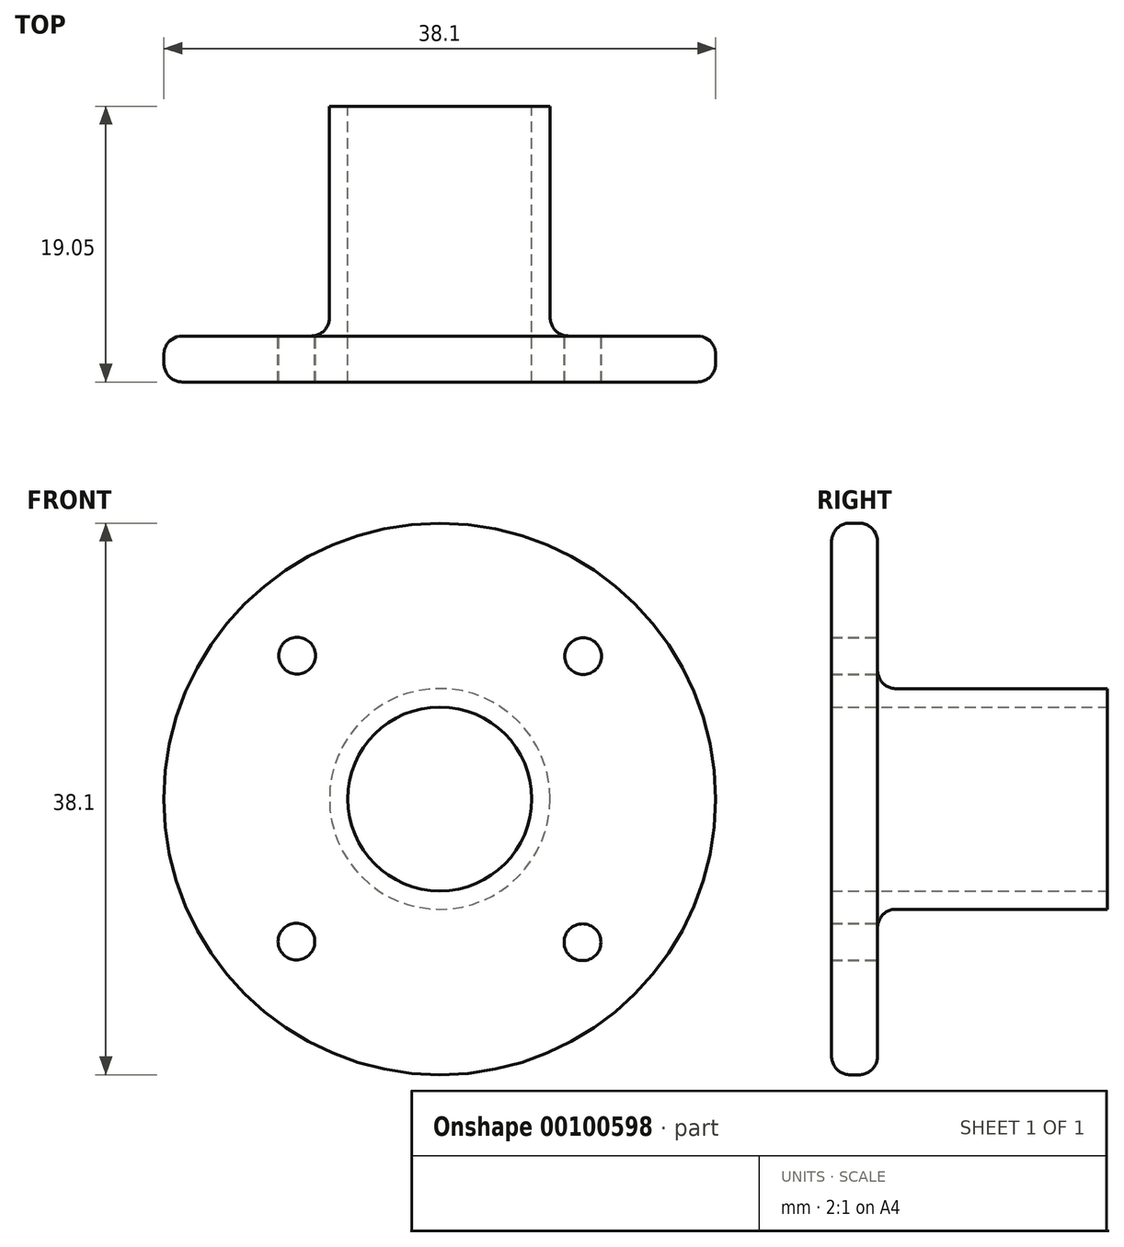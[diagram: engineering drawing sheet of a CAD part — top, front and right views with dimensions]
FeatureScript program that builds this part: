
annotation { "Feature Type Name" : "Feature", "Feature Type Description" : "" }
export const myFeature = defineFeature(function(context is Context, id is Id, definition is map)
    precondition{}
    {
        {
            var Q0;
            Q0=qCreatedBy(makeId("Front.planeOp"),FACE);
            var sketch = newSketch(context, id + "F0", { "sketchPlane" : qUnion([Q0])});
            skCircle(sketch, "E0", {"center": v(0, 0) * mm, "radius": 7.62 * mm});
            skSolve(sketch);
        }
        {
            var Q0;
            Q0=makeQuery(id+"F0.imprint","IMPRINT",FACE,{"disambiguationData":[TD([[makeQuery(id+"F0.imprint","IMPRINT",EDGE,{"derivedFrom":sQuery(id+"F0.wireOp",EDGE,"E0")}),1.0]])]});
            extrude(context, id + "F1", {"entities" : qUnion([Q0]), "depth" : 19.05 * mm});
        }
        {
            var Q0;
            Q0=makeQuery(id+"F1.opExtrude","CAP_FACE",FACE,{"disambiguationData":[OSD([sQuery(id+"F0.wireOp",EDGE,"E0")])],"isStart":false});
            var sketch = newSketch(context, id + "F2", { "sketchPlane" : qUnion([Q0])});
            skCircle(sketch, "E1", {"center": v(0, 0) * mm, "radius": 19.05 * mm});
            skSolve(sketch);
        }
        {
            var Q0;
            Q0=makeQuery(id+"F2.imprint","IMPRINT",FACE,{"disambiguationData":[TD([[makeQuery(id+"F2.imprint","IMPRINT",EDGE,{"derivedFrom":sQuery(id+"F2.wireOp",EDGE,"E1")}),1.0]])]});
            var Q1;
            Q1=makeQuery(id+"F2.imprint","IMPRINT",FACE,{"disambiguationData":[TD([[makeQuery(id+"F2.imprint","IMPRINT",EDGE,{"derivedFrom":makeQuery(id+"F1.opExtrude","CAP_EDGE",EDGE,{"disambiguationData":[OSD([sQuery(id+"F0.wireOp",EDGE,"E0")])],"isStart":false})}),1.0]])]});
            extrude(context, id + "F3", {"entities" : qUnion([Q0, Q1]), "operationType" : NewBodyOperationType.ADD, "oppositeDirection" : true, "depth" : 3.17 * mm});
        }
        {
            var Q0;
            Q0=sQuery(id+"F0.wireOp",VERTEX,"E0.center");
            var Q1;
            Q1=makeQuery(id+"F1.opExtrude","SWEPT_BODY",BODY,{"disambiguationData":[OSD([sQuery(id+"F0.wireOp",EDGE,"E0")])]});
            hole(context, id + "F4", {"style" : HoleStyle.SIMPLE, "endStyle" : HoleEndStyle.THROUGH, "oppositeDirection" : true, "holeDiameter" : 12.7 * mm, "locations" : qUnion([Q0]), "scope" : qUnion([Q1]), "isTappedThrough" : true});
        }
        {
            var Q0;
            Q0=makeQuery(id+"F3.opExtrude","CAP_EDGE",EDGE,{"disambiguationData":[OSD([sQuery(id+"F2.wireOp",EDGE,"E1")])],"isStart":false});
            var Q1;
            Q1=makeQuery(id+"F3.boolean.opBoolean","INTERSECT",EDGE,{"derivedFrom":[makeQuery(id+"F1.opExtrude","SWEPT_FACE",FACE,{"disambiguationData":[OSD([sQuery(id+"F0.wireOp",EDGE,"E0")])]}),makeQuery(id+"F3.opExtrude","CAP_FACE",FACE,{"disambiguationData":[OSD([sQuery(id+"F2.wireOp",EDGE,"E1")])],"isStart":false})]});
            var Q2;
            Q2=makeQuery(id+"F3.opExtrude","CAP_EDGE",EDGE,{"disambiguationData":[OSD([sQuery(id+"F2.wireOp",EDGE,"E1")])],"isStart":true});
            fillet(context, id + "F5", {"entities" : qUnion([Q0, Q1, Q2]), "radius" : 1.27 * mm, "tangentPropagation" : true, "allowEdgeOverflow" : false});
        }
        {
            var Q0;
            Q0=makeQuery(id+"F3.opExtrude","CAP_FACE",FACE,{"disambiguationData":[OSD([sQuery(id+"F2.wireOp",EDGE,"E1")])],"isStart":false});
            var sketch = newSketch(context, id + "F6", { "sketchPlane" : qUnion([Q0])});
            skPoint(sketch, "E2", {"position": v(-9.9, 9.86) * mm});
            skPoint(sketch, "E3.1.0", {"position": v(9.86, 9.9) * mm});
            skPoint(sketch, "E3.2.0", {"position": v(9.9, -9.86) * mm});
            skPoint(sketch, "E3.3.0", {"position": v(-9.86, -9.9) * mm});
            skPoint(sketch, "E3.center", {"position": v(0, 0) * mm});
            skLineSegment(sketch, "E3.anchor1", {"start": v(0, 0) * mm, "end": v(-9.9, 9.86) * mm, "construction": true});
            skLineSegment(sketch, "E3.anchor2", {"start": v(0, 0) * mm, "end": v(-9.86, -9.9) * mm, "construction": true});
            skSolve(sketch);
        }
        {
            var Q0;
            Q0=sQuery(id+"F6.wireOp",VERTEX,"E2");
            var Q1;
            Q1=sQuery(id+"F6.wireOp",VERTEX,"E3.1.0");
            var Q2;
            Q2=sQuery(id+"F6.wireOp",VERTEX,"E3.2.0");
            var Q3;
            Q3=sQuery(id+"F6.wireOp",VERTEX,"E3.3.0");
            var Q4;
            Q4=makeQuery(id+"F1.opExtrude","SWEPT_BODY",BODY,{"disambiguationData":[OSD([sQuery(id+"F0.wireOp",EDGE,"E0")])]});
            hole(context, id + "F7", {"style" : HoleStyle.SIMPLE, "endStyle" : HoleEndStyle.THROUGH, "holeDiameter" : 2.54 * mm, "locations" : qUnion([Q0, Q1, Q2, Q3]), "scope" : qUnion([Q4]), "isTappedThrough" : true});
        }
    });
